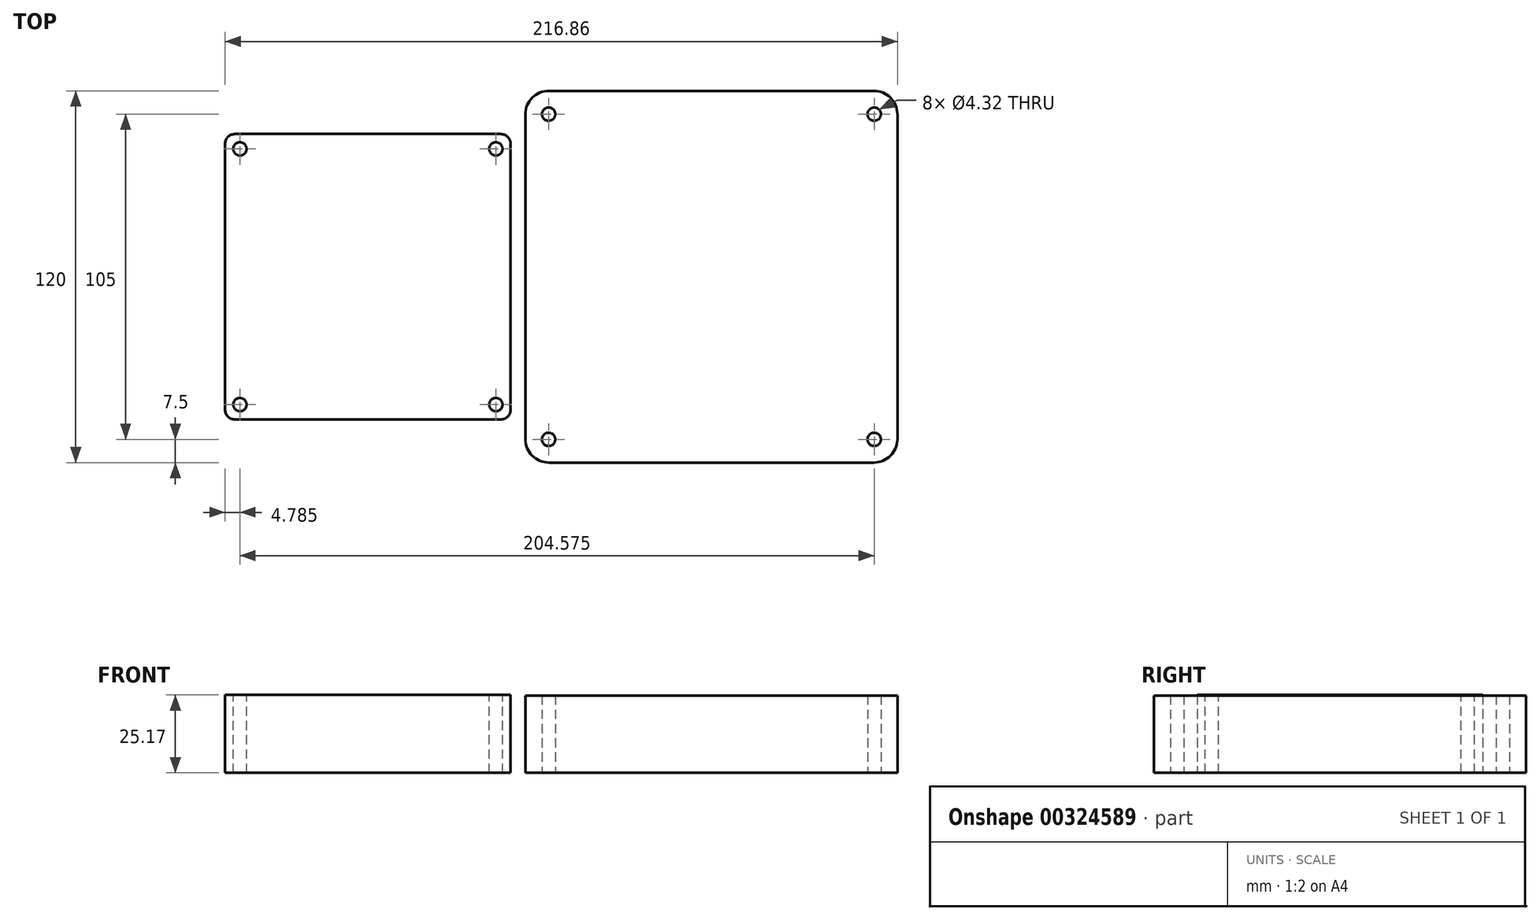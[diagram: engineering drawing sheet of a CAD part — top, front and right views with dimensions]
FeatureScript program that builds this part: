
annotation { "Feature Type Name" : "Feature", "Feature Type Description" : "" }
export const myFeature = defineFeature(function(context is Context, id is Id, definition is map)
    precondition{}
    {
        {
            var Q0;
            Q0=qCreatedBy(makeId("Top.planeOp"),FACE);
            var sketch = newSketch(context, id + "F0", { "sketchPlane" : qUnion([Q0])});
            skLineSegment(sketch, "E0.bottom", {"start": v(-42.89, 46.06) * mm, "end": v(42.89, 46.06) * mm});
            skLineSegment(sketch, "E0.top", {"start": v(-42.89, -46.06) * mm, "end": v(42.89, -46.06) * mm});
            skLineSegment(sketch, "E0.left", {"start": v(-46.06, 42.89) * mm, "end": v(-46.06, -42.89) * mm});
            skLineSegment(sketch, "E0.right", {"start": v(46.06, 42.89) * mm, "end": v(46.06, -42.89) * mm});
            skPoint(sketch, "E1.visualSharp", {"position": v(-46.06, 46.06) * mm});
            skArc(sketch, "E1.filletArc", {"start": v(-42.89, 46.06) * mm, "mid": v(-45.13, 45.13) * mm, "end": v(-46.06, 42.89) * mm});
            skPoint(sketch, "E2.visualSharp", {"position": v(46.06, 46.06) * mm});
            skArc(sketch, "E2.filletArc", {"start": v(46.06, 42.89) * mm, "mid": v(45.13, 45.13) * mm, "end": v(42.89, 46.06) * mm});
            skPoint(sketch, "E3.visualSharp", {"position": v(-46.06, -46.06) * mm});
            skArc(sketch, "E3.filletArc", {"start": v(-46.06, -42.89) * mm, "mid": v(-45.13, -45.13) * mm, "end": v(-42.89, -46.06) * mm});
            skPoint(sketch, "E4.visualSharp", {"position": v(46.06, -46.06) * mm});
            skArc(sketch, "E4.filletArc", {"start": v(42.89, -46.06) * mm, "mid": v(45.13, -45.13) * mm, "end": v(46.06, -42.89) * mm});
            skSolve(sketch);
        }
        {
            var Q0;
            Q0 = qSketchRegion(id + "F0", true);
            extrude(context, id + "F1", {"entities" : qUnion([Q0]), "depth" : 25.17 * mm});
        }
        {
            var Q0;
            Q0=makeQuery(id+"F1.opExtrude","CAP_FACE",FACE,{"disambiguationData":[OSD([sQuery(id+"F0.wireOp",EDGE,"E0.bottom"),sQuery(id+"F0.wireOp",EDGE,"E0.top"),sQuery(id+"F0.wireOp",EDGE,"E0.left"),sQuery(id+"F0.wireOp",EDGE,"E0.right"),sQuery(id+"F0.wireOp",EDGE,"E1.filletArc"),sQuery(id+"F0.wireOp",EDGE,"E2.filletArc"),sQuery(id+"F0.wireOp",EDGE,"E3.filletArc"),sQuery(id+"F0.wireOp",EDGE,"E4.filletArc")])],"isStart":false});
            var sketch = newSketch(context, id + "F2", { "sketchPlane" : qUnion([Q0])});
            skPoint(sketch, "E5", {"position": v(-41.28, 41.27) * mm});
            skPoint(sketch, "E6", {"position": v(41.28, 41.27) * mm});
            skPoint(sketch, "E7", {"position": v(-41.28, -41.27) * mm});
            skPoint(sketch, "E8", {"position": v(41.28, -41.27) * mm});
            skSolve(sketch);
        }
        {
            var Q0;
            Q0=sQuery(id+"F2.wireOp",VERTEX,"E5");
            var Q1;
            Q1=sQuery(id+"F2.wireOp",VERTEX,"E6");
            var Q2;
            Q2=sQuery(id+"F2.wireOp",VERTEX,"E7");
            var Q3;
            Q3=sQuery(id+"F2.wireOp",VERTEX,"E8");
            var Q4;
            Q4=makeQuery(id+"F1.opExtrude","SWEPT_BODY",BODY,{"disambiguationData":[OSD([sQuery(id+"F0.wireOp",EDGE,"E0.bottom"),sQuery(id+"F0.wireOp",EDGE,"E0.top"),sQuery(id+"F0.wireOp",EDGE,"E0.left"),sQuery(id+"F0.wireOp",EDGE,"E0.right"),sQuery(id+"F0.wireOp",EDGE,"E1.filletArc"),sQuery(id+"F0.wireOp",EDGE,"E2.filletArc"),sQuery(id+"F0.wireOp",EDGE,"E3.filletArc"),sQuery(id+"F0.wireOp",EDGE,"E4.filletArc")])]});
            hole(context, id + "F3", {"style" : HoleStyle.SIMPLE, "endStyle" : HoleEndStyle.THROUGH, "holeDiameter" : 4.32 * mm, "tappedDepth" : 12.7 * mm, "tapClearance" : 3, "locations" : qUnion([Q0, Q1, Q2, Q3]), "scope" : qUnion([Q4])});
        }
        {
            var Q0;
            Q0=qCreatedBy(makeId("Top.planeOp"),FACE);
            var sketch = newSketch(context, id + "F4", { "sketchPlane" : qUnion([Q0])});
            skLineSegment(sketch, "E9.bottom", {"start": v(50.8, 60) * mm, "end": v(170.8, 60) * mm});
            skLineSegment(sketch, "E9.top", {"start": v(50.8, -60) * mm, "end": v(170.8, -60) * mm});
            skLineSegment(sketch, "E9.left", {"start": v(50.8, 60) * mm, "end": v(50.8, -60) * mm});
            skLineSegment(sketch, "E9.right", {"start": v(170.8, 60) * mm, "end": v(170.8, -60) * mm});
            skPoint(sketch, "E10", {"position": v(170.8, 0) * mm});
            skLineSegment(sketch, "E11", {"start": v(110.8, 60) * mm, "end": v(110.8, -60) * mm, "construction": true});
            skLineSegment(sketch, "E12", {"start": v(170.8, 0) * mm, "end": v(50.8, 0) * mm, "construction": true});
            skCircle(sketch, "E13", {"center": v(58.3, 52.5) * mm, "radius": 2.16 * mm});
            skCircle(sketch, "E14", {"center": v(163.3, 52.5) * mm, "radius": 2.16 * mm});
            skCircle(sketch, "E15", {"center": v(58.3, -52.5) * mm, "radius": 2.16 * mm});
            skCircle(sketch, "E16", {"center": v(163.3, -52.5) * mm, "radius": 2.16 * mm});
            skSolve(sketch);
        }
        {
            var Q0;
            Q0=makeQuery(id+"F4.imprint","IMPRINT",FACE,{"disambiguationData":[TD([[makeQuery(id+"F4.imprint","IMPRINT",EDGE,{"derivedFrom":sQuery(id+"F4.wireOp",EDGE,"E9.bottom")}),-1.0]])]});
            extrude(context, id + "F5", {"entities" : qUnion([Q0]), "depth" : 25 * mm});
        }
        {
            var Q0;
            Q0=makeQuery(id+"F5.opExtrude","SWEPT_EDGE",EDGE,{"disambiguationData":[OSD([sQuery(id+"F4.wireOp",EDGE,"E9.top"),sQuery(id+"F4.wireOp",EDGE,"E9.left")])]});
            var Q1;
            Q1=makeQuery(id+"F5.opExtrude","SWEPT_EDGE",EDGE,{"disambiguationData":[OSD([sQuery(id+"F4.wireOp",EDGE,"E9.top"),sQuery(id+"F4.wireOp",EDGE,"E9.right")])]});
            var Q2;
            Q2=makeQuery(id+"F5.opExtrude","SWEPT_EDGE",EDGE,{"disambiguationData":[OSD([sQuery(id+"F4.wireOp",EDGE,"E9.bottom"),sQuery(id+"F4.wireOp",EDGE,"E9.right")])]});
            var Q3;
            Q3=makeQuery(id+"F5.opExtrude","SWEPT_EDGE",EDGE,{"disambiguationData":[OSD([sQuery(id+"F4.wireOp",EDGE,"E9.bottom"),sQuery(id+"F4.wireOp",EDGE,"E9.left")])]});
            fillet(context, id + "F6", {"entities" : qUnion([Q0, Q1, Q2, Q3]), "radius" : 7.62 * mm, "tangentPropagation" : true, "allowEdgeOverflow" : false});
        }
    });
